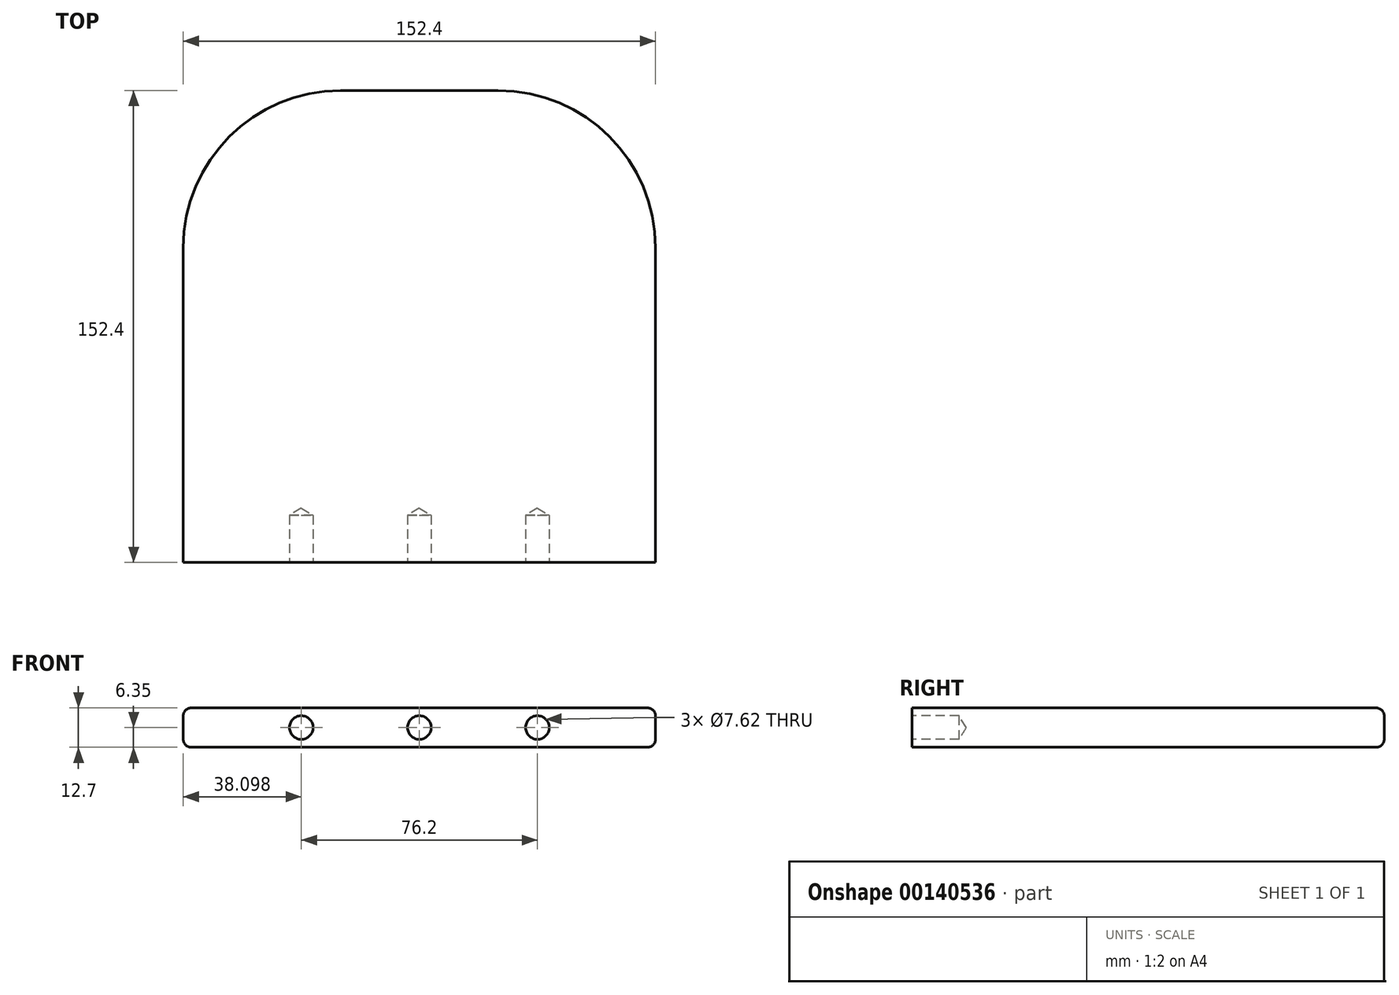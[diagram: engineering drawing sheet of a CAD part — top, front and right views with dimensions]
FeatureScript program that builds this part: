
annotation { "Feature Type Name" : "Feature", "Feature Type Description" : "" }
export const myFeature = defineFeature(function(context is Context, id is Id, definition is map)
    precondition{}
    {
        {
            var Q0;
            Q0=qCreatedBy(makeId("Top.planeOp"),FACE);
            var sketch = newSketch(context, id + "F0", { "sketchPlane" : qUnion([Q0])});
            skLineSegment(sketch, "E0.bottom", {"start": v(-74.22, 29.18) * mm, "end": v(78.18, 29.18) * mm});
            skLineSegment(sketch, "E0.top", {"start": v(-74.22, -123.22) * mm, "end": v(78.18, -123.22) * mm});
            skLineSegment(sketch, "E0.left", {"start": v(-74.22, 29.18) * mm, "end": v(-74.22, -123.22) * mm});
            skLineSegment(sketch, "E0.right", {"start": v(78.18, 29.18) * mm, "end": v(78.18, -123.22) * mm});
            skSolve(sketch);
        }
        {
            var Q0;
            Q0=makeQuery(id+"F0.imprint","IMPRINT",FACE,{"disambiguationData":[TD([[makeQuery(id+"F0.imprint","IMPRINT",EDGE,{"derivedFrom":sQuery(id+"F0.wireOp",EDGE,"E0.bottom")}),-1.0]])]});
            extrude(context, id + "F1", {"entities" : qUnion([Q0]), "depth" : 12.7 * mm});
        }
        {
            var Q0;
            Q0=makeQuery(id+"F1.opExtrude","SWEPT_EDGE",EDGE,{"disambiguationData":[OSD([sQuery(id+"F0.wireOp",EDGE,"E0.bottom"),sQuery(id+"F0.wireOp",EDGE,"E0.left")])]});
            var Q1;
            Q1=makeQuery(id+"F1.opExtrude","SWEPT_EDGE",EDGE,{"disambiguationData":[OSD([sQuery(id+"F0.wireOp",EDGE,"E0.bottom"),sQuery(id+"F0.wireOp",EDGE,"E0.right")])]});
            fillet(context, id + "F2", {"entities" : qUnion([Q0, Q1]), "radius" : 50.8 * mm, "tangentPropagation" : true, "allowEdgeOverflow" : false});
        }
        {
            var Q0;
            Q0=makeQuery(id+"F1.opExtrude","SWEPT_FACE",FACE,{"disambiguationData":[OSD([sQuery(id+"F0.wireOp",EDGE,"E0.top")])]});
            var sketch = newSketch(context, id + "F3", { "sketchPlane" : qUnion([Q0])});
            skLineSegment(sketch, "E1.bottom", {"start": v(78.18, 0) * mm, "end": v(-74.22, 0) * mm});
            skLineSegment(sketch, "E1.top", {"start": v(78.18, 12.7) * mm, "end": v(-74.22, 12.7) * mm});
            skLineSegment(sketch, "E1.left", {"start": v(78.18, 0) * mm, "end": v(78.18, 12.7) * mm});
            skLineSegment(sketch, "E1.right", {"start": v(-74.22, 0) * mm, "end": v(-74.22, 12.7) * mm});
            skLineSegment(sketch, "E2", {"start": v(1.98, 12.7) * mm, "end": v(1.98, 0) * mm});
            skLineSegment(sketch, "E3", {"start": v(1.98, 0) * mm, "end": v(-74.22, 0) * mm});
            skLineSegment(sketch, "E4", {"start": v(-36.12, 0) * mm, "end": v(-36.12, 12.7) * mm});
            skLineSegment(sketch, "E5", {"start": v(-36.12, 12.7) * mm, "end": v(-36.12, 0) * mm});
            skLineSegment(sketch, "E6", {"start": v(1.98, 12.7) * mm, "end": v(78.18, 12.7) * mm});
            skLineSegment(sketch, "E7", {"start": v(40.08, 12.7) * mm, "end": v(40.08, 0) * mm});
            skLineSegment(sketch, "E8", {"start": v(40.08, 0) * mm, "end": v(40.08, 12.7) * mm});
            skPoint(sketch, "E9", {"position": v(1.98, 6.35) * mm});
            skPoint(sketch, "E10", {"position": v(40.08, 6.35) * mm});
            skPoint(sketch, "E11", {"position": v(-36.12, 6.35) * mm});
            skCircle(sketch, "E12", {"center": v(40.08, 6.35) * mm, "radius": 3.81 * mm});
            skCircle(sketch, "E13", {"center": v(1.98, 6.35) * mm, "radius": 3.81 * mm});
            skCircle(sketch, "E14", {"center": v(-36.12, 6.35) * mm, "radius": 3.81 * mm});
            skSolve(sketch);
        }
        {
            var Q0;
            Q0=sQuery(id+"F3.wireOp",VERTEX,"E10");
            var Q1;
            Q1=sQuery(id+"F3.wireOp",VERTEX,"E9");
            var Q2;
            Q2=sQuery(id+"F3.wireOp",VERTEX,"E11");
            var Q3;
            Q3=makeQuery(id+"F1.opExtrude","SWEPT_BODY",BODY,{"disambiguationData":[OSD([sQuery(id+"F0.wireOp",EDGE,"E0.bottom"),sQuery(id+"F0.wireOp",EDGE,"E0.top"),sQuery(id+"F0.wireOp",EDGE,"E0.left"),sQuery(id+"F0.wireOp",EDGE,"E0.right")])]});
            hole(context, id + "F4", {"style" : HoleStyle.SIMPLE, "endStyle" : HoleEndStyle.BLIND, "holeDiameter" : 7.62 * mm, "holeDepth" : 15.24 * mm, "locations" : qUnion([Q0, Q1, Q2]), "scope" : qUnion([Q3])});
        }
        {
            var Q0;
            Q0=makeQuery(id+"F1.opExtrude","CAP_EDGE",EDGE,{"disambiguationData":[OSD([sQuery(id+"F0.wireOp",EDGE,"E0.right")])],"isStart":false});
            var Q1;
            Q1=makeQuery(id+"F1.opExtrude","CAP_EDGE",EDGE,{"disambiguationData":[OSD([sQuery(id+"F0.wireOp",EDGE,"E0.right")])],"isStart":true});
            fillet(context, id + "F5", {"entities" : qUnion([Q0, Q1]), "radius" : 2.54 * mm, "tangentPropagation" : true, "allowEdgeOverflow" : false});
        }
    });
